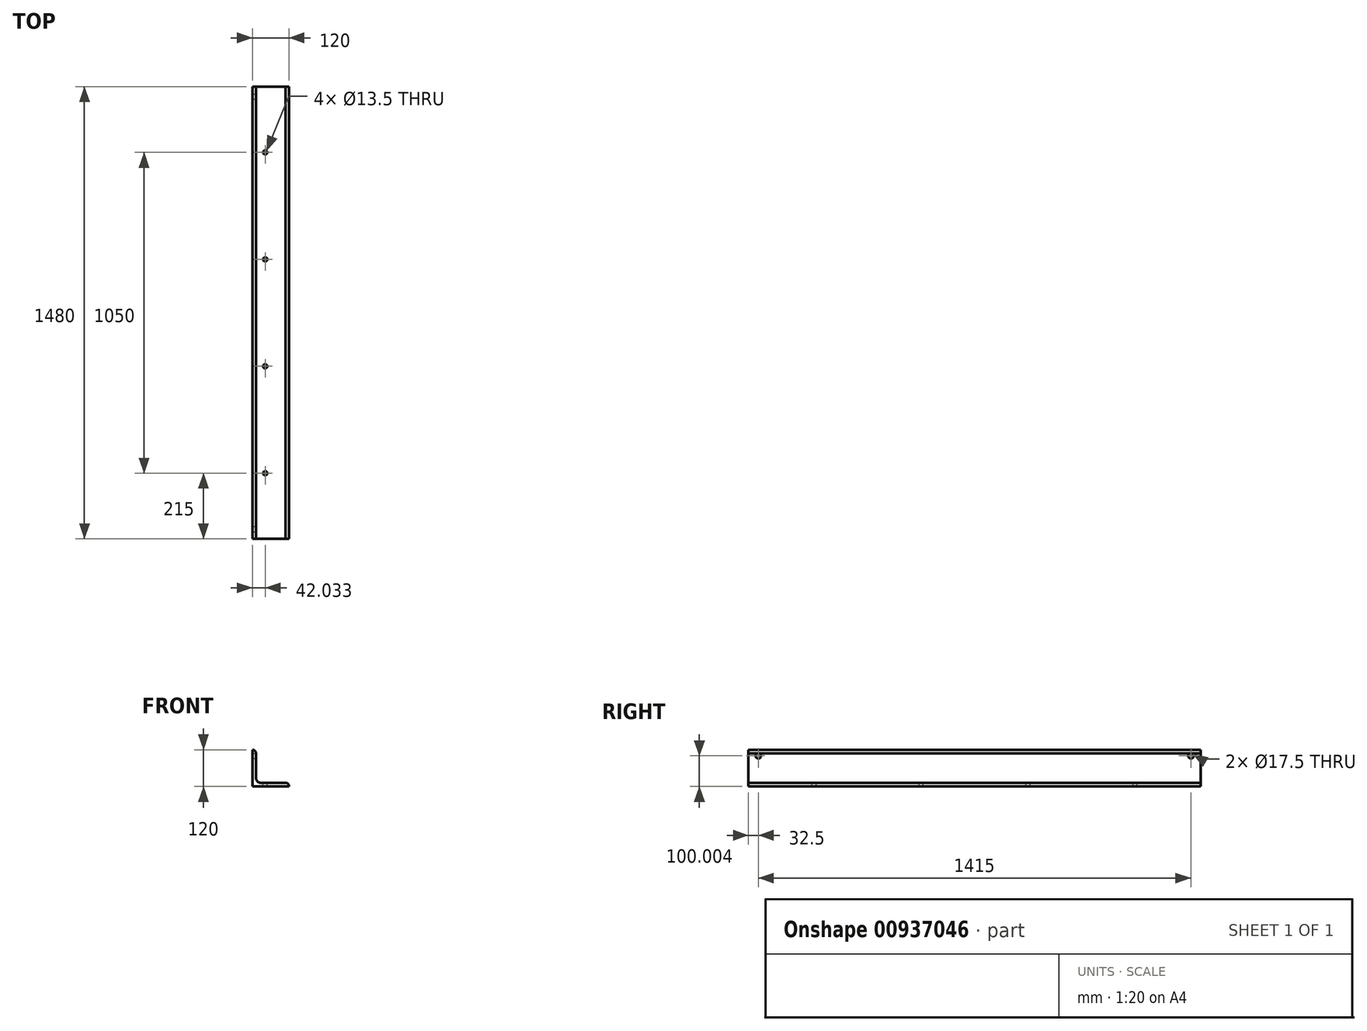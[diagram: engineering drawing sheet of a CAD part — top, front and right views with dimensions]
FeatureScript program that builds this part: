
annotation { "Feature Type Name" : "Feature", "Feature Type Description" : "" }
export const myFeature = defineFeature(function(context is Context, id is Id, definition is map)
    precondition{}
    {
        {
            var Q0;
            Q0=qCreatedBy(makeId("Top.planeOp"),FACE);
            var sketch = newSketch(context, id + "F0", { "sketchPlane" : qUnion([Q0])});
            skLineSegment(sketch, "E0", {"start": v(0, 0) * mm, "end": v(0, 1480) * mm});
            skSolve(sketch);
        }
        {
            var Q0;
            Q0=qCreatedBy(makeId("Front.planeOp"),FACE);
            var sketch = newSketch(context, id + "F1", { "sketchPlane" : qUnion([Q0])});
            skLineSegment(sketch, "E1.bottom", {"start": v(0, 0) * mm, "end": v(120, 0) * mm});
            skLineSegment(sketch, "E1.left", {"start": v(0, 0) * mm, "end": v(0, 120) * mm});
            skLineSegment(sketch, "E2.bottom", {"start": v(27.04, 12.05) * mm, "end": v(108.47, 12) * mm});
            skLineSegment(sketch, "E2.left", {"start": v(12.05, 27.04) * mm, "end": v(12, 108.47) * mm});
            skLineSegment(sketch, "E3", {"start": v(0, 0) * mm, "end": v(120, 120) * mm, "construction": true});
            skPoint(sketch, "E4", {"position": v(60, 60) * mm});
            skPoint(sketch, "E5.visualSharp", {"position": v(12.06, 12.06) * mm});
            skArc(sketch, "E5.filletArc", {"start": v(12.05, 27.04) * mm, "mid": v(16.44, 16.44) * mm, "end": v(27.04, 12.05) * mm});
            skPoint(sketch, "E6.orphan", {"position": v(108.01, 108.01) * mm});
            skArc(sketch, "E7", {"start": v(12, 108.47) * mm, "mid": v(8.32, 116.65) * mm, "end": v(0, 120) * mm});
            skArc(sketch, "E8.MirrorCS", {"start": v(108.47, 12) * mm, "mid": v(116.65, 8.32) * mm, "end": v(120, 0) * mm});
            skSolve(sketch);
        }
        {
            var Q0;
            Q0 = qSketchRegion(id + "F1", true);
            extrude(context, id + "F2", {"entities" : qUnion([Q0]), "oppositeDirection" : true, "depth" : 1480 * mm, "offsetDistance" : 25 * mm});
        }
        {
            var Q0;
            Q0=makeQuery(id+"F2.opExtrude","SWEPT_FACE",FACE,{"disambiguationData":[OSD([sQuery(id+"F1.wireOp",EDGE,"E2.left")])]});
            var sketch = newSketch(context, id + "F3", { "sketchPlane" : qUnion([Q0])});
            skLineSegment(sketch, "E9", {"start": v(740, 108.46) * mm, "end": v(740, -76.97) * mm, "construction": true});
            skPoint(sketch, "E10", {"position": v(32.5, 100) * mm});
            skPoint(sketch, "E11.MirrorP", {"position": v(1447.5, 100) * mm});
            skSolve(sketch);
        }
        {
            var Q0;
            Q0=sQuery(id+"F3.wireOp",VERTEX,"E10");
            var Q1;
            Q1=sQuery(id+"F3.wireOp",VERTEX,"E11.MirrorP");
            var Q2;
            Q2=makeQuery(id+"F2.opExtrude","SWEPT_BODY",BODY,{"disambiguationData":[OSD([sQuery(id+"F1.wireOp",EDGE,"E1.bottom"),sQuery(id+"F1.wireOp",EDGE,"E1.left"),sQuery(id+"F1.wireOp",EDGE,"E2.bottom"),sQuery(id+"F1.wireOp",EDGE,"E2.left"),sQuery(id+"F1.wireOp",EDGE,"E5.filletArc"),sQuery(id+"F1.wireOp",EDGE,"E7"),sQuery(id+"F1.wireOp",EDGE,"E8.MirrorCS")])]});
            hole(context, id + "F4", {"style" : HoleStyle.SIMPLE, "endStyle" : HoleEndStyle.THROUGH, "standardTappedOrClearance" : lookupTablePath({ "fit" : "Normal", "standard" : "ISO", "size" : "M16", "type" : "Clearance" }), "standardBlindInLast" : lookupTablePath({ "fit" : "Normal", "standard" : "ISO", "engagement" : "75%", "pitch" : "2 mm", "size" : "M16", "type" : "Clearance & tapped" }), "holeDiameter" : 17.5 * mm, "majorDiameter" : 5 * mm, "isTappedThrough" : true, "tappedDepth" : 12 * mm, "tapClearance" : 3, "startFromSketch" : true, "locations" : qUnion([Q0, Q1]), "scope" : qUnion([Q2])});
        }
        {
            var Q0;
            Q0=makeQuery(id+"F2.opExtrude","SWEPT_FACE",FACE,{"disambiguationData":[OSD([sQuery(id+"F1.wireOp",EDGE,"E2.bottom")])]});
            var sketch = newSketch(context, id + "F5", { "sketchPlane" : qUnion([Q0])});
            skLineSegment(sketch, "E12", {"start": v(42.03, 1480) * mm, "end": v(42.03, -215.73) * mm, "construction": true});
            skPoint(sketch, "E13", {"position": v(42.03, 215) * mm});
            skPoint(sketch, "E14.0.1.0", {"position": v(42.03, 565) * mm});
            skPoint(sketch, "E14.0.2.0", {"position": v(42.03, 915) * mm});
            skPoint(sketch, "E14.0.3.0", {"position": v(42.03, 1265) * mm});
            skLineSegment(sketch, "E14.direction1", {"start": v(42.03, 215) * mm, "end": v(257.03, 215) * mm, "construction": true});
            skLineSegment(sketch, "E14.direction2", {"start": v(42.03, 215) * mm, "end": v(42.03, 565) * mm, "construction": true});
            skSolve(sketch);
        }
        {
            var Q0;
            Q0=sQuery(id+"F5.wireOp",VERTEX,"E13");
            var Q1;
            Q1=sQuery(id+"F5.wireOp",VERTEX,"E14.0.1.0");
            var Q2;
            Q2=sQuery(id+"F5.wireOp",VERTEX,"E14.0.2.0");
            var Q3;
            Q3=sQuery(id+"F5.wireOp",VERTEX,"E14.0.3.0");
            var Q4;
            Q4=makeQuery(id+"F2.opExtrude","SWEPT_BODY",BODY,{"disambiguationData":[OSD([sQuery(id+"F1.wireOp",EDGE,"E1.bottom"),sQuery(id+"F1.wireOp",EDGE,"E1.left"),sQuery(id+"F1.wireOp",EDGE,"E2.bottom"),sQuery(id+"F1.wireOp",EDGE,"E2.left"),sQuery(id+"F1.wireOp",EDGE,"E5.filletArc"),sQuery(id+"F1.wireOp",EDGE,"E7"),sQuery(id+"F1.wireOp",EDGE,"E8.MirrorCS")])]});
            hole(context, id + "F6", {"style" : HoleStyle.SIMPLE, "endStyle" : HoleEndStyle.THROUGH, "standardTappedOrClearance" : lookupTablePath({ "fit" : "Normal", "standard" : "ISO", "size" : "M12", "type" : "Clearance" }), "standardBlindInLast" : lookupTablePath({ "fit" : "Normal", "standard" : "ISO", "engagement" : "75%", "pitch" : "1.75 mm", "size" : "M12", "type" : "Clearance & tapped" }), "holeDiameter" : 13.5 * mm, "majorDiameter" : 5 * mm, "isTappedThrough" : true, "tappedDepth" : 12 * mm, "tapClearance" : 3, "startFromSketch" : true, "locations" : qUnion([Q0, Q1, Q2, Q3]), "scope" : qUnion([Q4])});
        }
    });
